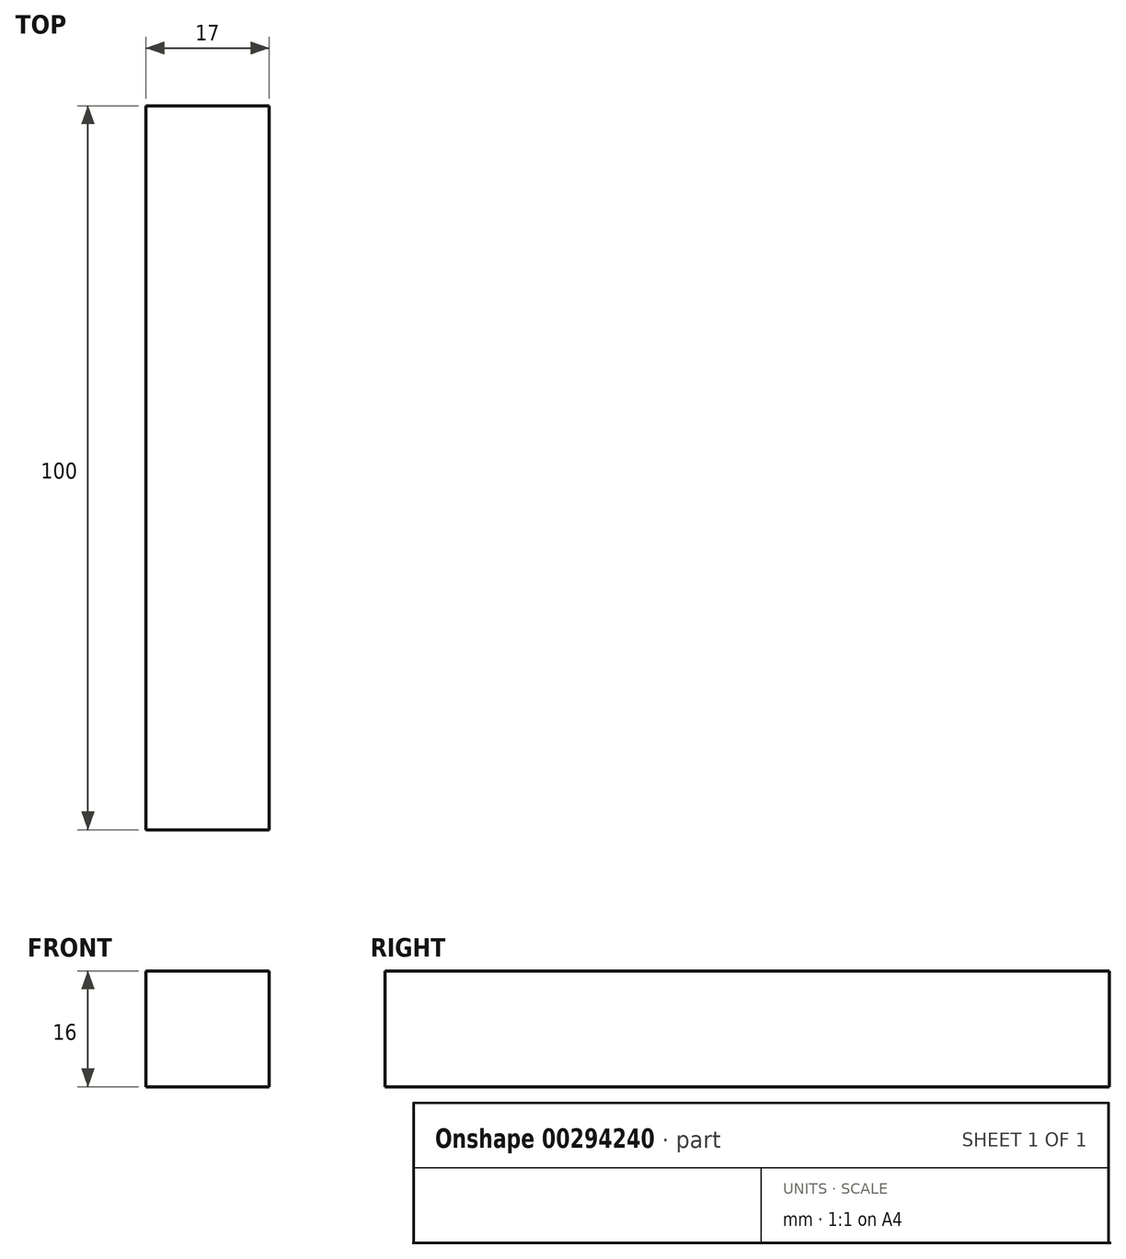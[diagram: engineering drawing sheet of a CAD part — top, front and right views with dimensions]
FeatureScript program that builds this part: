
annotation { "Feature Type Name" : "Feature", "Feature Type Description" : "" }
export const myFeature = defineFeature(function(context is Context, id is Id, definition is map)
    precondition{}
    {
        {
            var Q0;
            Q0=qCreatedBy(makeId("Front.planeOp"),FACE);
            var sketch = newSketch(context, id + "F0", { "sketchPlane" : qUnion([Q0])});
            skLineSegment(sketch, "E0.bottom", {"start": v(8.5, 8) * mm, "end": v(-8.5, 8) * mm});
            skLineSegment(sketch, "E0.top", {"start": v(8.5, -8) * mm, "end": v(-8.5, -8) * mm});
            skLineSegment(sketch, "E0.left", {"start": v(8.5, 8) * mm, "end": v(8.5, -8) * mm});
            skLineSegment(sketch, "E0.right", {"start": v(-8.5, 8) * mm, "end": v(-8.5, -8) * mm});
            skPoint(sketch, "E0.middle", {"position": v(0, 0) * mm});
            skLineSegment(sketch, "E1", {"start": v(8.5, 5.46) * mm, "end": v(-2.25, 5.46) * mm});
            skLineSegment(sketch, "E2", {"start": v(-2.25, 5.46) * mm, "end": v(-2.25, -6.54) * mm});
            skLineSegment(sketch, "E3", {"start": v(-2.25, -6.54) * mm, "end": v(8.5, -6.54) * mm});
            skSolve(sketch);
        }
        {
            var Q0;
            Q0 = qSketchRegion(id + "F0", true);
            extrude(context, id + "F1", {"entities" : qUnion([Q0]), "depth" : 100 * mm});
        }
    });
